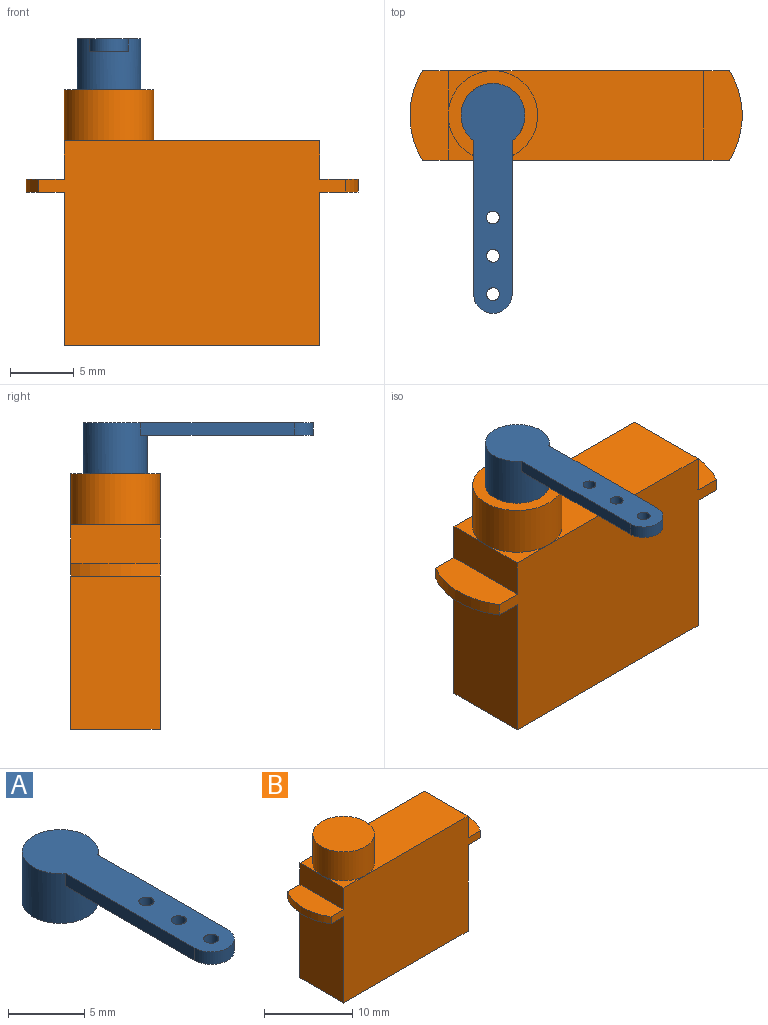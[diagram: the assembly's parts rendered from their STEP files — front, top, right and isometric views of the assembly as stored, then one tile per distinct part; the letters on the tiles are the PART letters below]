
ASSEMBLY  parts=2 mates=1
PART A: 10 faces, bbox 5x18x4 mm
  f0: cylinder r=2.5mm len=5mm, axis (0,0,-1), area 59.6mm2, adj f1,f2,f4,f6,f9
  f1: plane 5x5mm, normal (0,0,-1), area 19.6mm2, adj f0
  f2: plane 13.5x3mm, normal (0,0,-1), area 36.2mm2, adj f0,f3,f4,f5,f6,f7,f8
  f3: cylinder r=1.5mm len=3mm, axis (0,0,-1), area 4.7mm2, adj f2,f4,f6,f9
  f4: plane 12x1mm, normal (1,0,0), area 12mm2, adj f0,f2,f3,f9
  f5: cylinder r=0.5mm len=1mm, axis (0,0,-1), area 3.1mm2, adj f2,f9
  f6: plane 12x1mm, normal (-1,0,0), area 12mm2, adj f0,f2,f3,f9
  f7: cylinder r=0.5mm len=1mm, axis (0,0,-1), area 3.1mm2, adj f2,f9
  f8: cylinder r=0.5mm len=1mm, axis (0,0,-1), area 3.1mm2, adj f2,f9
  f9: plane 18x5mm, normal (0,0,1), area 55.8mm2, adj f0,f3,f4,f5,f6,f7,f8
PART B: 18 faces, bbox 26x7x20 mm
  f0: plane 3.5x3.5mm, normal (0,0,1), area 2.6mm2, adj f3,f4,f16
  f1: plane 3.5x3.5mm, normal (0,0,1), area 2.6mm2, adj f3,f6,f16
  f2: plane 7x3mm, normal (1,0,0), area 21mm2, adj f4,f6,f9,f14
  f3: plane 7x3mm, normal (-1,0,0), area 21mm2, adj f0,f1,f4,f6,f11
  f4: plane 24x16mm, normal (0,1,0), area 324mm2, adj f0,f2,f3,f5,f7,f8,f9,f10
  f5: plane 12x7mm, normal (-1,0,0), area 84mm2, adj f4,f6,f8,f12
  f6: plane 24x16mm, normal (0,-1,0), area 324mm2, adj f1,f2,f3,f5,f7,f8,f9,f10
  f7: plane 12x7mm, normal (1,0,0), area 84mm2, adj f4,f6,f8,f15
  f8: plane 20x7mm, normal (0,0,-1), area 140mm2, adj f4,f5,f6,f7
  f9: plane 16.5x7mm, normal (0,0,1), area 96.3mm2, adj f2,f4,f6,f16
  f10: cylinder r=6.62mm len=7mm, axis (0,0,-1), area 7.4mm2, adj f4,f6,f11,f12
  f11: plane 7x3mm, normal (0,0,1), area 18.7mm2, adj f3,f4,f6,f10
  f12: plane 7x3mm, normal (0,0,-1), area 18.7mm2, adj f4,f5,f6,f10
  f13: cylinder r=6.62mm len=7mm, axis (0,0,-1), area 7.4mm2, adj f4,f6,f14,f15
  f14: plane 7x3mm, normal (0,0,1), area 18.7mm2, adj f2,f4,f6,f13
  f15: plane 7x3mm, normal (0,0,-1), area 18.7mm2, adj f4,f6,f7,f13
  f16: cylinder r=3.5mm len=7mm, axis (0,0,-1), area 88mm2, adj f0,f1,f9,f17
  f17: plane 7x7mm, normal (0,0,1), area 38.5mm2, adj f16
PLACE A t=(-11.39,0.9,7.3)mm
PLACE B t=(-11.39,0.9,-0.7)mm
MATE revolute A.f0 <-> B.f16  axis (0,0,-1) through (-7.89,-2.6,7.3)mm
